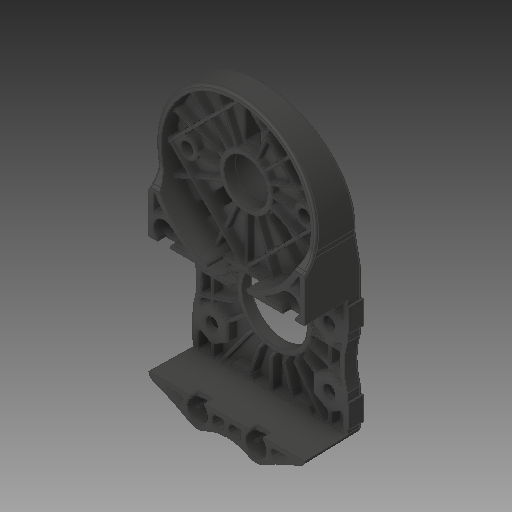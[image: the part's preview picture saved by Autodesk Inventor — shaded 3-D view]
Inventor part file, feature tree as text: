
AUTODESK INVENTOR PART (.ipt)
format: ipt  version: 2018 (Build 220112000, 112)  size: 5,430,272 bytes
history: native  units: in
note: dims shown in document units (in); Inventor stores cm internally (conversion verified against a paired STEP export)
features: chamfer x1
ambient origin geometry x8: Origin, YZ Plane, XZ Plane, XY Plane, X Axis, Y Axis, Z Axis, Center Point
bodies: Solid1 (feature_tree)
feature tree (1):
  chamfer  "Chamfer2"  [1 undecoded]
note: 1 required parameter value undecoded (feature->parameter linkage not recoverable at this tier; creation-order binding heuristic only, values carry confidence <= 0.55)
